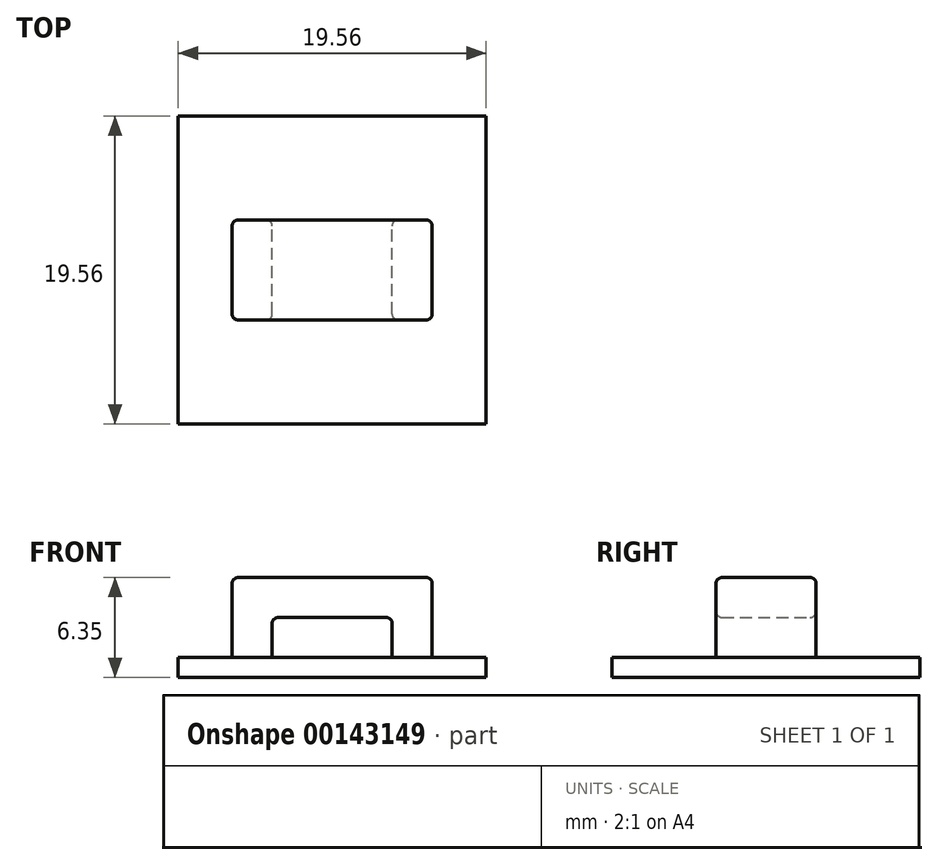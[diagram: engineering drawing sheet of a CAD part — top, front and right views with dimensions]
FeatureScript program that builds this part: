
annotation { "Feature Type Name" : "Feature", "Feature Type Description" : "" }
export const myFeature = defineFeature(function(context is Context, id is Id, definition is map)
    precondition{}
    {
        {
            var Q0;
            Q0=qCreatedBy(makeId("Front.planeOp"),FACE);
            var sketch = newSketch(context, id + "F0", { "sketchPlane" : qUnion([Q0])});
            skLineSegment(sketch, "E0.bottom", {"start": v(-3.81, 1.27) * mm, "end": v(3.81, 1.27) * mm});
            skLineSegment(sketch, "E0.top", {"start": v(-3.81, -1.27) * mm, "end": v(3.81, -1.27) * mm});
            skLineSegment(sketch, "E0.left", {"start": v(-3.81, 1.27) * mm, "end": v(-3.81, -1.27) * mm});
            skLineSegment(sketch, "E0.right", {"start": v(3.81, 1.27) * mm, "end": v(3.81, -1.27) * mm});
            skLineSegment(sketch, "E1", {"start": v(0, 1.27) * mm, "end": v(0, -1.27) * mm, "construction": true});
            skLineSegment(sketch, "E2", {"start": v(-3.81, 0) * mm, "end": v(3.81, 0) * mm, "construction": true});
            skPoint(sketch, "E3", {"position": v(0, 0) * mm});
            skLineSegment(sketch, "E4.0", {"start": v(-6.35, 3.81) * mm, "end": v(6.35, 3.81) * mm});
            skLineSegment(sketch, "E4.1", {"start": v(-6.35, 3.81) * mm, "end": v(-6.35, -3.81) * mm});
            skLineSegment(sketch, "E4.2", {"start": v(-6.35, -3.81) * mm, "end": v(6.35, -3.81) * mm});
            skLineSegment(sketch, "E4.3", {"start": v(6.35, 3.81) * mm, "end": v(6.35, -3.81) * mm});
            skLineSegment(sketch, "E5", {"start": v(-3.81, -1.27) * mm, "end": v(-6.35, -1.27) * mm});
            skLineSegment(sketch, "E6", {"start": v(3.81, -1.27) * mm, "end": v(6.35, -1.27) * mm});
            skSolve(sketch);
        }
        {
            var Q0;
            Q0=makeQuery(id+"F0.imprint","IMPRINT",FACE,{"disambiguationData":[TD([[makeQuery(id+"F0.imprint","IMPRINT",EDGE,{"derivedFrom":sQuery(id+"F0.wireOp",EDGE,"E0.bottom")}),1.0]])]});
            extrude(context, id + "F1", {"entities" : qUnion([Q0]), "endBound" : BoundingType.SYMMETRIC, "depth" : 6.35 * mm});
        }
        {
            var Q0;
            Q0=makeQuery(id+"F1.opExtrude","CAP_EDGE",EDGE,{"disambiguationData":[OSD([sQuery(id+"F0.wireOp",EDGE,"E4.0")])],"isStart":true});
            var Q1;
            Q1=makeQuery(id+"F1.opExtrude","SWEPT_EDGE",EDGE,{"disambiguationData":[OSD([sQuery(id+"F0.wireOp",EDGE,"E4.0"),sQuery(id+"F0.wireOp",EDGE,"E4.3")])]});
            var Q2;
            Q2=makeQuery(id+"F1.opExtrude","CAP_EDGE",EDGE,{"disambiguationData":[OSD([sQuery(id+"F0.wireOp",EDGE,"E4.0")])],"isStart":false});
            var Q3;
            Q3=makeQuery(id+"F1.opExtrude","SWEPT_EDGE",EDGE,{"disambiguationData":[OSD([sQuery(id+"F0.wireOp",EDGE,"E4.0"),sQuery(id+"F0.wireOp",EDGE,"E4.1")])]});
            var Q4;
            Q4=makeQuery(id+"F1.opExtrude","CAP_EDGE",EDGE,{"disambiguationData":[OSD([sQuery(id+"F0.wireOp",EDGE,"E4.1")])],"isStart":false});
            var Q5;
            Q5=makeQuery(id+"F1.opExtrude","CAP_EDGE",EDGE,{"disambiguationData":[OSD([sQuery(id+"F0.wireOp",EDGE,"E4.1")])],"isStart":true});
            var Q6;
            Q6=makeQuery(id+"F1.opExtrude","CAP_EDGE",EDGE,{"disambiguationData":[OSD([sQuery(id+"F0.wireOp",EDGE,"E0.bottom")])],"isStart":true});
            var Q7;
            Q7=makeQuery(id+"F1.opExtrude","CAP_EDGE",EDGE,{"disambiguationData":[OSD([sQuery(id+"F0.wireOp",EDGE,"E0.left")])],"isStart":true});
            var Q8;
            Q8=makeQuery(id+"F1.opExtrude","CAP_EDGE",EDGE,{"disambiguationData":[OSD([sQuery(id+"F0.wireOp",EDGE,"E0.right")])],"isStart":true});
            var Q9;
            Q9=makeQuery(id+"F1.opExtrude","CAP_EDGE",EDGE,{"disambiguationData":[OSD([sQuery(id+"F0.wireOp",EDGE,"E4.3")])],"isStart":true});
            var Q10;
            Q10=makeQuery(id+"F1.opExtrude","CAP_EDGE",EDGE,{"disambiguationData":[OSD([sQuery(id+"F0.wireOp",EDGE,"E4.3")])],"isStart":false});
            var Q11;
            Q11=makeQuery(id+"F1.opExtrude","CAP_EDGE",EDGE,{"disambiguationData":[OSD([sQuery(id+"F0.wireOp",EDGE,"E0.bottom")])],"isStart":false});
            var Q12;
            Q12=makeQuery(id+"F1.opExtrude","CAP_EDGE",EDGE,{"disambiguationData":[OSD([sQuery(id+"F0.wireOp",EDGE,"E0.left")])],"isStart":false});
            var Q13;
            Q13=makeQuery(id+"F1.opExtrude","CAP_EDGE",EDGE,{"disambiguationData":[OSD([sQuery(id+"F0.wireOp",EDGE,"E0.right")])],"isStart":false});
            var Q14;
            Q14=makeQuery(id+"F1.opExtrude","SWEPT_EDGE",EDGE,{"disambiguationData":[OSD([sQuery(id+"F0.wireOp",EDGE,"E0.bottom"),sQuery(id+"F0.wireOp",EDGE,"E0.left")])]});
            var Q15;
            Q15=makeQuery(id+"F1.opExtrude","SWEPT_EDGE",EDGE,{"disambiguationData":[OSD([sQuery(id+"F0.wireOp",EDGE,"E0.bottom"),sQuery(id+"F0.wireOp",EDGE,"E0.right")])]});
            fillet(context, id + "F2", {"entities" : qUnion([Q0, Q1, Q2, Q3, Q4, Q5, Q6, Q7, Q8, Q9, Q10, Q11, Q12, Q13, Q14, Q15]), "radius" : 0.38 * mm, "tangentPropagation" : true, "allowEdgeOverflow" : false});
        }
        {
            var Q0;
            Q0=makeQuery(id+"F1.opExtrude","SWEPT_FACE",FACE,{"disambiguationData":[OSD([sQuery(id+"F0.wireOp",EDGE,"E6")])]});
            var sketch = newSketch(context, id + "F3", { "sketchPlane" : qUnion([Q0])});
            skLineSegment(sketch, "E7.bottom", {"start": v(9.78, 9.78) * mm, "end": v(-9.78, 9.78) * mm});
            skLineSegment(sketch, "E7.top", {"start": v(9.78, -9.78) * mm, "end": v(-9.78, -9.78) * mm});
            skLineSegment(sketch, "E7.left", {"start": v(9.78, 9.78) * mm, "end": v(9.78, -9.78) * mm});
            skLineSegment(sketch, "E7.right", {"start": v(-9.78, 9.78) * mm, "end": v(-9.78, -9.78) * mm});
            skPoint(sketch, "E7.middle", {"position": v(0, 0) * mm});
            skSolve(sketch);
        }
        {
            var Q0;
            Q0=makeQuery(id+"F3.imprint","IMPRINT",FACE,{"disambiguationData":[TD([[makeQuery(id+"F3.imprint","IMPRINT",EDGE,{"derivedFrom":sQuery(id+"F3.wireOp",EDGE,"E7.bottom")}),1.0]])]});
            var Q1;
            {var subQ0=sQuery(id+"F0.wireOp",EDGE,"E6");Q1=makeQuery(id+"F3.imprint","IMPRINT",FACE,{"disambiguationData":[TD([[makeQuery(id+"F3.imprint","IMPRINT",EDGE,{"derivedFrom":makeQuery(id+"F1.opExtrude","CAP_EDGE",EDGE,{"disambiguationData":[OSD([subQ0])],"isStart":true})}),1.0]])]});}
            extrude(context, id + "F4", {"entities" : qUnion([Q0, Q1]), "operationType" : NewBodyOperationType.ADD, "depth" : 1.27 * mm});
        }
    });
